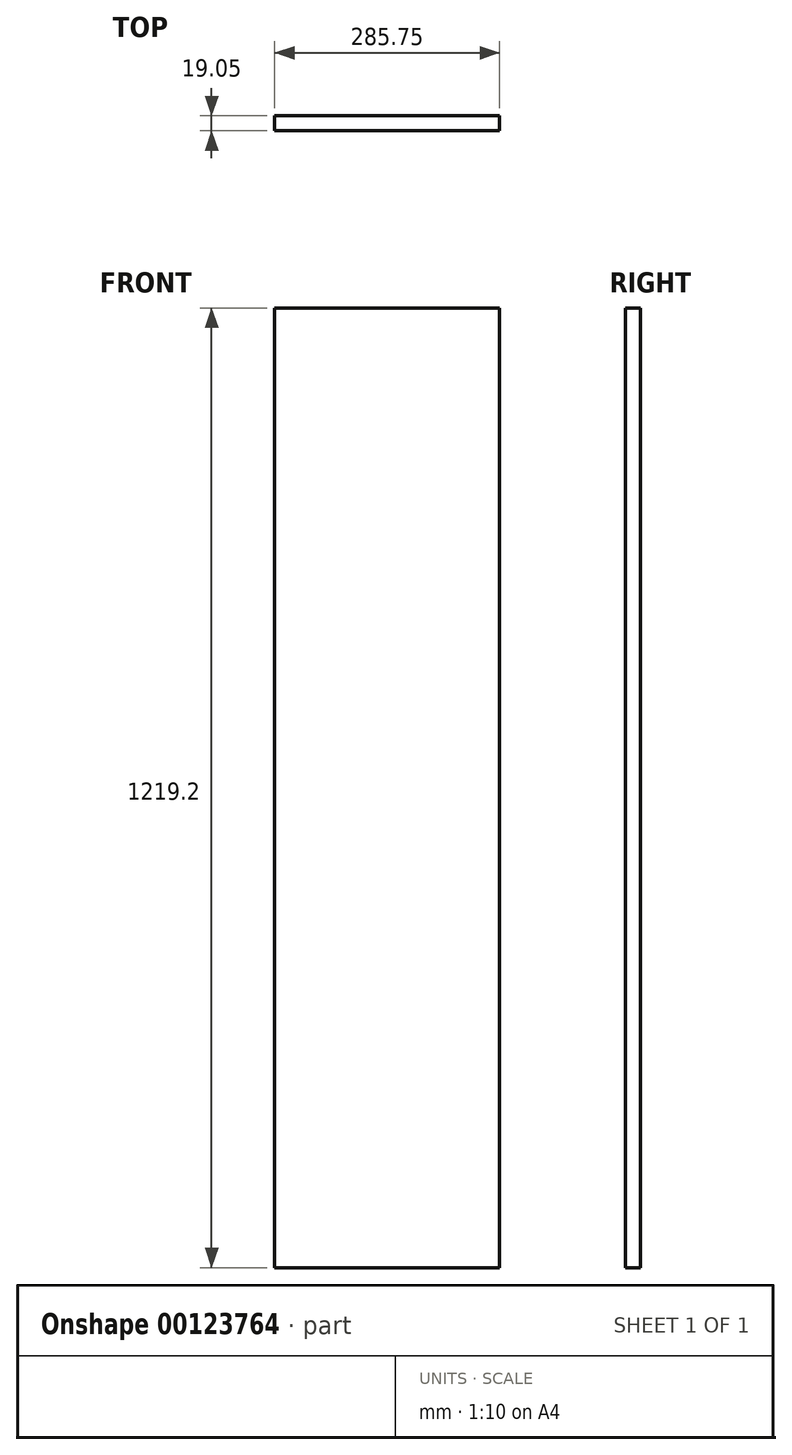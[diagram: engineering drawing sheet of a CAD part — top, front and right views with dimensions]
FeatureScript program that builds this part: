
annotation { "Feature Type Name" : "Feature", "Feature Type Description" : "" }
export const myFeature = defineFeature(function(context is Context, id is Id, definition is map)
    precondition{}
    {
        {
            var Q0;
            Q0=qCreatedBy(makeId("Front.planeOp"),FACE);
            var sketch = newSketch(context, id + "F0", { "sketchPlane" : qUnion([Q0])});
            skLineSegment(sketch, "E0.bottom", {"start": v(-183.93, 1021.05) * mm, "end": v(101.82, 1021.05) * mm});
            skLineSegment(sketch, "E0.top", {"start": v(-183.93, -198.15) * mm, "end": v(101.82, -198.15) * mm});
            skLineSegment(sketch, "E0.left", {"start": v(-183.93, 1021.05) * mm, "end": v(-183.93, -198.15) * mm});
            skLineSegment(sketch, "E0.right", {"start": v(101.82, 1021.05) * mm, "end": v(101.82, -198.15) * mm});
            skSolve(sketch);
        }
        {
            var Q0;
            Q0 = qSketchRegion(id + "F0", true);
            extrude(context, id + "F1", {"entities" : qUnion([Q0]), "depth" : 19.05 * mm});
        }
    });
